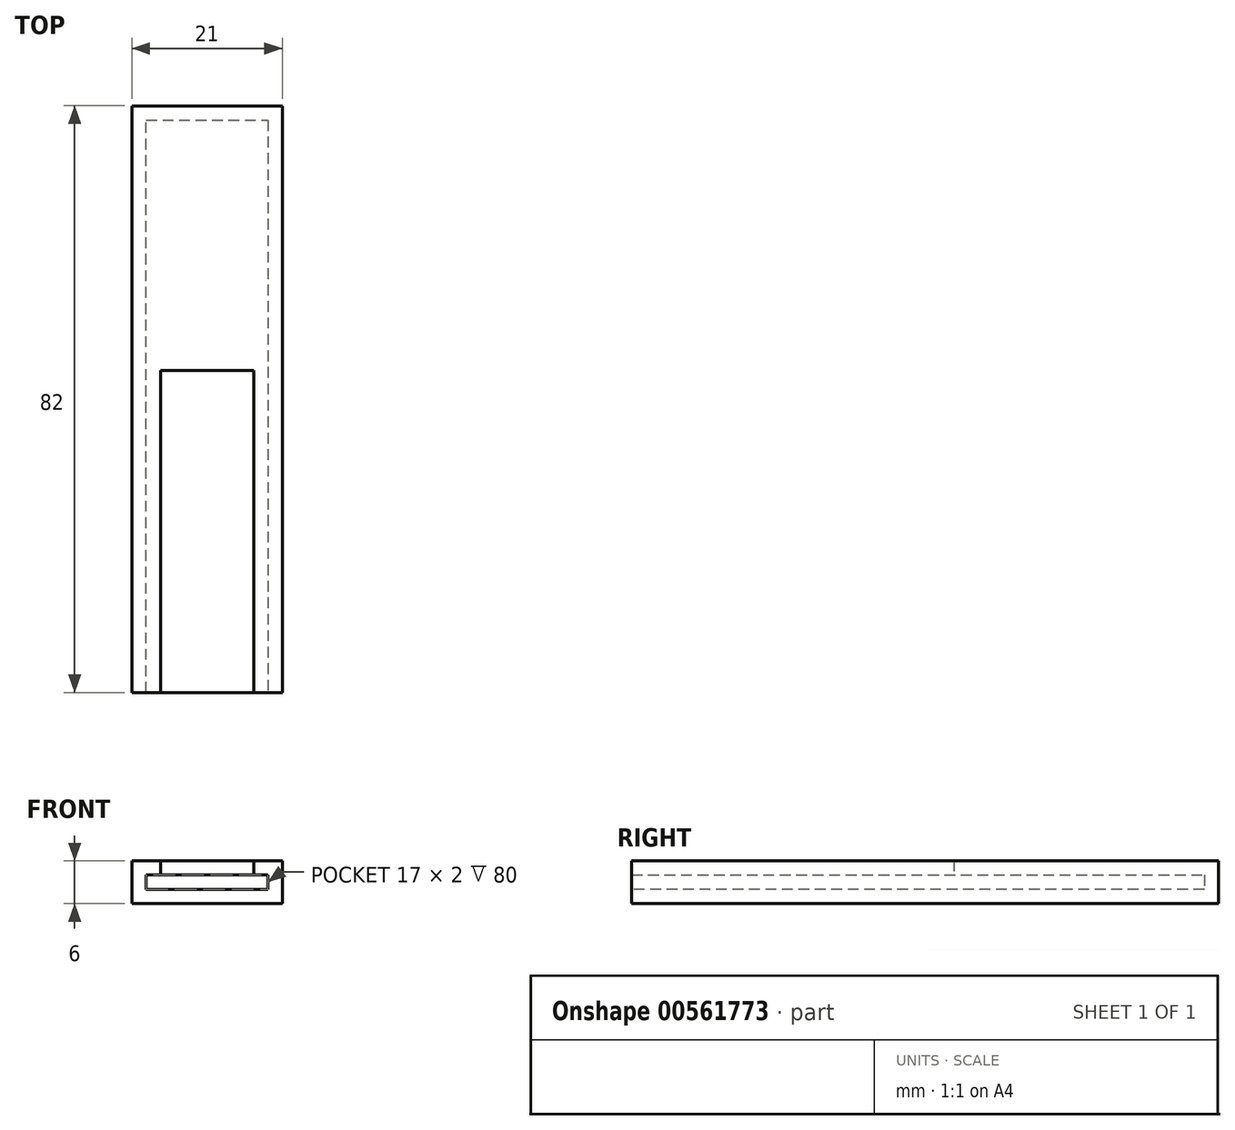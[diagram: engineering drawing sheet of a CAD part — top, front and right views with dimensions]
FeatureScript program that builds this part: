
annotation { "Feature Type Name" : "Feature", "Feature Type Description" : "" }
export const myFeature = defineFeature(function(context is Context, id is Id, definition is map)
    precondition{}
    {
        {
            var Q0;
            Q0=qCreatedBy(makeId("Top.planeOp"),FACE);
            var sketch = newSketch(context, id + "F0", { "sketchPlane" : qUnion([Q0])});
            skLineSegment(sketch, "E0", {"start": v(-31.54, 43.1) * mm, "end": v(-31.54, -38.9) * mm});
            skLineSegment(sketch, "E1", {"start": v(-31.54, -38.9) * mm, "end": v(-10.54, -38.9) * mm});
            skLineSegment(sketch, "E2", {"start": v(-10.54, -38.9) * mm, "end": v(-10.54, 43.1) * mm});
            skLineSegment(sketch, "E3", {"start": v(-10.54, 43.1) * mm, "end": v(-31.54, 43.1) * mm});
            skSolve(sketch);
        }
        {
            var Q0;
            Q0=makeQuery(id+"F0.imprint","IMPRINT",FACE,{"disambiguationData":[TD([[makeQuery(id+"F0.imprint","IMPRINT",EDGE,{"derivedFrom":sQuery(id+"F0.wireOp",EDGE,"E0")}),1.0]])]});
            extrude(context, id + "F1", {"entities" : qUnion([Q0]), "depth" : 2 * mm, "offsetDistance" : 25 * mm});
        }
        {
            var Q0;
            Q0=makeQuery(id+"F1.opExtrude","CAP_FACE",FACE,{"disambiguationData":[OSD([sQuery(id+"F0.wireOp",EDGE,"E0"),sQuery(id+"F0.wireOp",EDGE,"E1"),sQuery(id+"F0.wireOp",EDGE,"E2"),sQuery(id+"F0.wireOp",EDGE,"E3")])],"isStart":false});
            var sketch = newSketch(context, id + "F2", { "sketchPlane" : qUnion([Q0])});
            skLineSegment(sketch, "E4.0", {"start": v(-10.54, -38.9) * mm, "end": v(-10.54, 43.1) * mm});
            skLineSegment(sketch, "E5.0", {"start": v(-10.54, 43.1) * mm, "end": v(-31.54, 43.1) * mm});
            skLineSegment(sketch, "E6.0", {"start": v(-31.54, 43.1) * mm, "end": v(-31.54, -38.9) * mm});
            skLineSegment(sketch, "E7", {"start": v(-31.54, -38.9) * mm, "end": v(-29.54, -38.9) * mm});
            skLineSegment(sketch, "E8", {"start": v(-29.54, -38.9) * mm, "end": v(-29.54, 41.1) * mm});
            skLineSegment(sketch, "E9", {"start": v(-29.54, 41.1) * mm, "end": v(-12.54, 41.1) * mm});
            skLineSegment(sketch, "E10", {"start": v(-12.54, 41.1) * mm, "end": v(-12.54, -38.9) * mm});
            skLineSegment(sketch, "E11", {"start": v(-12.54, -38.9) * mm, "end": v(-10.54, -38.9) * mm});
            skSolve(sketch);
        }
        {
            var Q0;
            Q0=makeQuery(id+"F2.imprint","IMPRINT",FACE,{"disambiguationData":[TD([[makeQuery(id+"F2.imprint","IMPRINT",EDGE,{"derivedFrom":sQuery(id+"F2.wireOp",EDGE,"E4.0")}),1.0]])]});
            extrude(context, id + "F3", {"entities" : qUnion([Q0]), "operationType" : NewBodyOperationType.ADD, "depth" : 2 * mm, "offsetDistance" : 25 * mm});
        }
        {
            var Q0;
            Q0=makeQuery(id+"F3.opExtrude","CAP_FACE",FACE,{"disambiguationData":[OSD([sQuery(id+"F2.wireOp",EDGE,"E4.0"),sQuery(id+"F2.wireOp",EDGE,"E5.0"),sQuery(id+"F2.wireOp",EDGE,"E6.0"),sQuery(id+"F2.wireOp",EDGE,"E7"),sQuery(id+"F2.wireOp",EDGE,"E8"),sQuery(id+"F2.wireOp",EDGE,"E9"),sQuery(id+"F2.wireOp",EDGE,"E10"),sQuery(id+"F2.wireOp",EDGE,"E11")])],"isStart":false});
            cPlane(context, id + "F4", {"entities" : qUnion([Q0]), "cplaneType" : CPlaneType.OFFSET, "offset" : 0 * mm, "width" : 150 * mm, "height" : 150 * mm});
        }
        {
            var Q0;
            Q0=qCreatedBy(id+"F4.planeOp",FACE);
            var sketch = newSketch(context, id + "F5", { "sketchPlane" : qUnion([Q0])});
            skLineSegment(sketch, "E12.0", {"start": v(-10.54, 43.1) * mm, "end": v(-31.54, 43.1) * mm});
            skLineSegment(sketch, "E13.0", {"start": v(-31.54, 43.1) * mm, "end": v(-31.54, -38.9) * mm});
            skLineSegment(sketch, "E14.0", {"start": v(-10.54, -38.9) * mm, "end": v(-10.54, 43.1) * mm});
            skLineSegment(sketch, "E15", {"start": v(-31.54, 43.1) * mm, "end": v(-31.54, 0) * mm});
            skLineSegment(sketch, "E16", {"start": v(-31.54, 43.1) * mm, "end": v(-31.54, 8.1) * mm});
            skLineSegment(sketch, "E17", {"start": v(-10.54, 43.1) * mm, "end": v(-10.54, 8.1) * mm});
            skLineSegment(sketch, "E18", {"start": v(-10.54, -38.9) * mm, "end": v(-14.54, -38.9) * mm});
            skLineSegment(sketch, "E19", {"start": v(-14.54, -38.9) * mm, "end": v(-14.54, 6.1) * mm});
            skLineSegment(sketch, "E20", {"start": v(-14.54, 6.1) * mm, "end": v(-27.54, 6.1) * mm});
            skLineSegment(sketch, "E21", {"start": v(-27.54, 6.1) * mm, "end": v(-27.54, -38.9) * mm});
            skLineSegment(sketch, "E22", {"start": v(-27.54, -38.9) * mm, "end": v(-31.54, -38.9) * mm});
            skSolve(sketch);
        }
        {
            var Q0;
            Q0=makeQuery(id+"F5.imprint","IMPRINT",FACE,{"disambiguationData":[TD([[makeQuery(id+"F5.imprint","IMPRINT",EDGE,{"derivedFrom":sQuery(id+"F5.wireOp",EDGE,"E12.0")}),1.0]])]});
            extrude(context, id + "F6", {"entities" : qUnion([Q0]), "operationType" : NewBodyOperationType.ADD, "depth" : 2 * mm, "offsetDistance" : 25 * mm});
        }
    });
